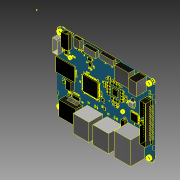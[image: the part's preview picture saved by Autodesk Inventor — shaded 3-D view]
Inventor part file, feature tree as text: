
AUTODESK INVENTOR PART (.ipt)
format: ipt  version: 2015 (Build 190159000, 159)  size: 3,793,408 bytes
history: native  units: in
note: dims shown in document units (in); Inventor stores cm internally (conversion verified against a paired STEP export)
features: sketch x4, other x3, extrude x2, fillet x1, hole x1, projected_geometry x1
ambient origin geometry x8: Origin, YZ Plane, XZ Plane, XY Plane, X Axis, Y Axis, Z Axis, Center Point
bodies: Solid1 (feature_tree)
feature tree (12):
  other  "[3D] ODROID-XU"
  extrude  "Extrusion1"  Depth=2.748in
  sketch  "Sketch4"  dims[d9=2.748in d10=0.0394in d11=0.0in]
  fillet  "Fillet1"  Radius=3.7008in
  extrude  "Extrusion2"  Depth=0.0394in TaperAngle=0.0deg
  hole  "Hole1"  [1 undecoded]
  sketch  "Sketch2"  dims[d0=3.7008in d1=2.748in d8=3.7008in]
  sketch  "Sketch5"  dims[d12=0.1339in d13=0.0394in d14=0.0in]
  projected_geometry  "Projected Loop1"
  sketch  "Sketch6"  dims[d15=3.4252in d16=2.748in d17=3.7008in d18=3.4252in d19=3.4252in d20=2.4803in d21=2.4803in d22=0.1575in d23=0.1575in d24=0.1575in d25=0.1575in d26=0.1417in d27=0.2953in d28=0.248in d29=0.0984in d30=90.0deg d31=0.3937in d32=0.8108in]
  other  "MeshFeature1"
  other  "Srf1"
note: 1 required parameter value undecoded (feature->parameter linkage not recoverable at this tier; creation-order binding heuristic only, values carry confidence <= 0.55)
